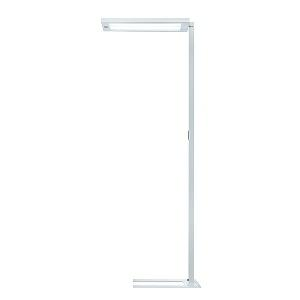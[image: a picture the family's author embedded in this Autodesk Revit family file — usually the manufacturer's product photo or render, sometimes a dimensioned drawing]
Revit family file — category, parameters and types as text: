
# Revit family: lavigo_-_dps_15000_840_r_g2a_00808520_90b2
name_source: partatom
category: Lighting Fixtures
units: mm (PartAtom-declared; Revit-internal decimal feet)

## family parameters
Cut with Voids When Loaded = No
Host = Face
Light Source = No
Part Type = Normal
Room Calculation Point = No
Round Connector Dimension = Use Diameter
Shared = No

## types (1)
- LAVIGO - DPS 15000/840/R/G2A (1 x LED, 15250 lm, 4000K)
    Apparent Load = 105 VA
    Approval mark = CE
    CIE Flux Codes = 60 87 97 11 100
    Color Rendering = 80-89
    Color Temperature = 4000K
    Control Gear = Electronic ballast
    Default Elevation = 1800 mm
    Description = DPS 15000/840/R/G2A|Free-standing luminaire|light source: LED|work equipment: Electronic ballast|connected load: 220-240 V, 50/60 Hz|Power consumption: approx. 105 W|standby: approx. 0,50|power factor: approx. 0,965|luminous flux: 15250 lm|luminous efficacy: 145 lm/W|light distribution: Direct/indirect|direct ratio: approx. 12 %|colour temperature: Cold white, ca. 4000 K|color rendering index (CRI): >= 80|chromaticity tolerance:  3 SDCM|technology: Presence and daylight sensor control (PIR)|operation: Multi-function switch|luminaire body|material: Steel/plastic|surface: Painted|colour: White|lamp cover: Acrylic (PMMA), Satine|tubular section|material: Steel tube|surface: Painted|Form: Tubular section upright|colour of tubular section: White|luminaire base|Form: C-form flat|weight (net): approx. 19.7 kg|mains lead: 3.00 m Mains plug CEE 7/VII|Fastening: Floor standing base|decorative contrast side parts: Flint grey|glare control: Prism aperture|luminance(L65): <= 3000 cd/m|unified glare rating(4H 8H): <=  16|special features: Luminaire head detachable, Asymmetric radiation, Cradle to Cradle Certified TM, Direct light component with edge light and light-guide technology for homogenous light exit, Flicker-free, Integrated light and presence sensor PIR, Retrofittable with TALK module, Separated, direct and indirect light individually adjustable|
    Height = 36 mm
    Lamp = 1 x LED
    Lamp Light Flux = 15250 lm
    Lamp count = 1
    Length = 675 mm
    Luminous efficacy = 145 lm/W
    Manufacturer = Waldmann
    ModVariant = No
    Model = 00808520
    Mounting Place = Floor
    Mounting Type = Freestanding
    Number of Poles = 1
    OnlyDefault = Yes
    Power Factor = 1
    Product Name = LAVIGO - DPS 15000/840/R/G2A
    Product group = Free standing luminaire
    ProductGroupID = 13
    Protection Class = Protection class I
    Protection Degree = IP 20
    RLX_Detail_Level = 1
    RLX_Emergency_Light_Flux = 0 lm
    RLX_Emergency_Type = 0
    RLX_Emergency_Type_DB = No
    RlxData = <blob elided: 42189 chars, md5=a713e319>
    Socket = socket
    Standby Power = 0 W
    System Light Flux = 15250 lm
    System Power = 105 W
    Type Comments = Product without accessories
    Type Image = 121695000-00610208.jpg
    URL = http://relux.com
    VarID = ---
    Voltage = 0 V
    Weight = 0.00 kg
    Width = 320 mm

## geometry (parser evidence)
native form markers: Blend x4, Sweep x14
no freeform markers — native parametric forms only
